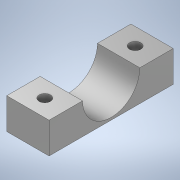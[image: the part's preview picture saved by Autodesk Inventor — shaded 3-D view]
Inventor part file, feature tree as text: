
AUTODESK INVENTOR PART (.ipt)
format: ipt  version: 2020 (Build 240168000, 168)  size: 120,320 bytes
history: native  units: mm
features: extrude x2, sketch x2, other x1
ambient origin geometry x8: Origin, YZ Plane, XZ Plane, XY Plane, X Axis, Y Axis, Z Axis, Center Point
bodies: Body1 (feature_tree)
feature tree (5):
  other  "Твердое тело1"
  extrude  "Выдавливание1"  Depth=15.0mm
  extrude  "Выдавливание2"  Depth=44.0mm
  sketch  "Эскиз1"
  sketch  "Эскиз2"
